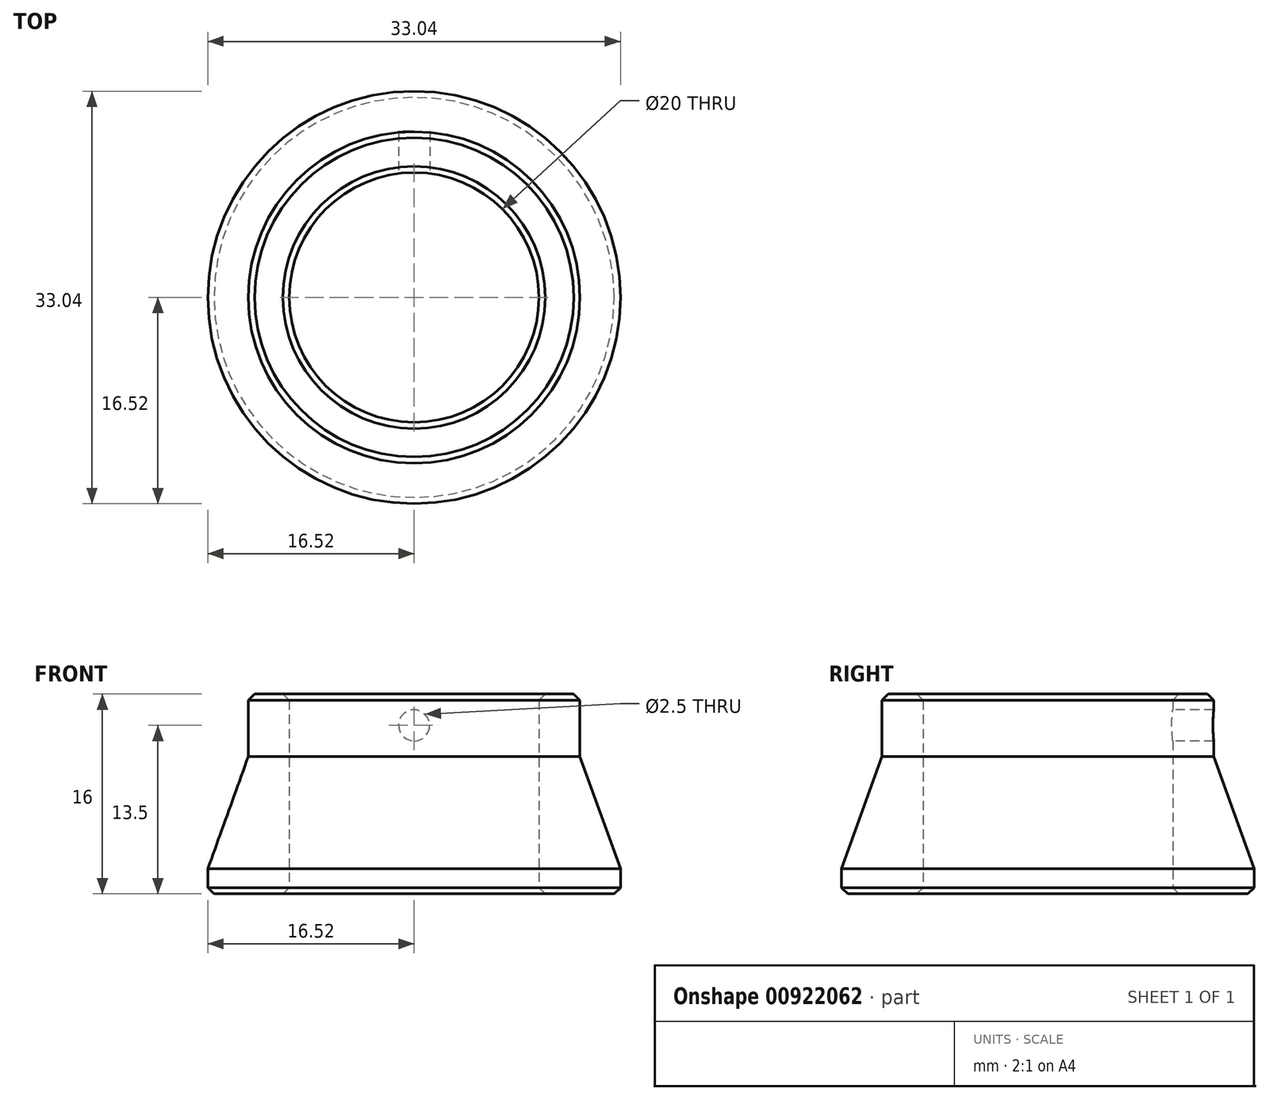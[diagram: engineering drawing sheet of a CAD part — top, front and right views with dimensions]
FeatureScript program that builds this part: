
annotation { "Feature Type Name" : "Feature", "Feature Type Description" : "" }
export const myFeature = defineFeature(function(context is Context, id is Id, definition is map)
    precondition{}
    {
        {
            var Q0;
            Q0=qCreatedBy(makeId("Front.planeOp"),FACE);
            var sketch = newSketch(context, id + "F0", { "sketchPlane" : qUnion([Q0])});
            skLineSegment(sketch, "E0", {"start": v(10, 0) * mm, "end": v(16.52, 0) * mm});
            skLineSegment(sketch, "E1", {"start": v(16.52, 0) * mm, "end": v(16.52, 2) * mm});
            skLineSegment(sketch, "E2", {"start": v(13.28, 15.77) * mm, "end": v(13.28, 16) * mm});
            skLineSegment(sketch, "E3", {"start": v(13.28, 16) * mm, "end": v(10, 16) * mm});
            skLineSegment(sketch, "E4", {"start": v(10, 16) * mm, "end": v(10, 0) * mm});
            skLineSegment(sketch, "E5", {"start": v(13.28, 15.77) * mm, "end": v(13.28, 11) * mm});
            skLineSegment(sketch, "E6", {"start": v(13.28, 11) * mm, "end": v(16.52, 2) * mm});
            skLineSegment(sketch, "E7", {"start": v(0, 0) * mm, "end": v(0, 44.28) * mm, "construction": true});
            skSolve(sketch);
        }
        {
            var Q0;
            Q0=makeQuery(id+"F0.imprint","IMPRINT",FACE,{"disambiguationData":[TD([[makeQuery(id+"F0.imprint","IMPRINT",EDGE,{"derivedFrom":sQuery(id+"F0.wireOp",EDGE,"E0")}),1.0]])]});
            var Q1;
            Q1=sQuery(id+"F0.wireOp",EDGE,"E7");
            revolve(context, id + "F1", {"surfaceOperationType" : NewSurfaceOperationType.NEW, "entities" : qUnion([Q0]), "axis" : qUnion([Q1]), "revolveType" : RevolveType.FULL});
        }
        {
            var Q0;
            Q0=qCreatedBy(makeId("Front.planeOp"),FACE);
            var sketch = newSketch(context, id + "F2", { "sketchPlane" : qUnion([Q0])});
            skPoint(sketch, "E8", {"position": v(0, 13.5) * mm});
            skSolve(sketch);
        }
        {
            var Q0;
            Q0=sQuery(id+"F2.wireOp",VERTEX,"E8");
            var Q1;
            Q1=makeQuery(id+"F1.opRevolve","SWEPT_BODY",BODY,{"disambiguationData":[OSD([sQuery(id+"F0.wireOp",EDGE,"E0"),sQuery(id+"F0.wireOp",EDGE,"E1"),sQuery(id+"F0.wireOp",EDGE,"E2"),sQuery(id+"F0.wireOp",EDGE,"E3"),sQuery(id+"F0.wireOp",EDGE,"E4"),sQuery(id+"F0.wireOp",EDGE,"E5"),sQuery(id+"F0.wireOp",EDGE,"E6")])]});
            hole(context, id + "F3", {"style" : HoleStyle.SIMPLE, "endStyle" : HoleEndStyle.THROUGH, "standardTappedOrClearance" : lookupTablePath({ "standard" : "ISO", "engagement" : "75%", "pitch" : "0.5 mm", "size" : "M3", "type" : "Tapped" }), "standardBlindInLast" : lookupTablePath({ "standard" : "ISO", "engagement" : "75%", "pitch" : "0.5 mm", "size" : "M3", "type" : "Tapped" }), "holeDiameter" : 2.5 * mm, "majorDiameter" : 3 * mm, "showTappedDepth" : true, "isTappedThrough" : true, "tappedDepth" : 6 * mm, "tapClearance" : 3, "locations" : qUnion([Q0]), "scope" : qUnion([Q1])});
        }
        {
            var Q0;
            Q0=makeQuery(id+"F1.opRevolve","SWEPT_EDGE",EDGE,{"disambiguationData":[OSD([sQuery(id+"F0.wireOp",EDGE,"E2"),sQuery(id+"F0.wireOp",EDGE,"E3")])]});
            var Q1;
            Q1=makeQuery(id+"F1.opRevolve","SWEPT_EDGE",EDGE,{"disambiguationData":[OSD([sQuery(id+"F0.wireOp",EDGE,"E3"),sQuery(id+"F0.wireOp",EDGE,"E4")])]});
            var Q2;
            Q2=makeQuery(id+"F1.opRevolve","SWEPT_EDGE",EDGE,{"disambiguationData":[OSD([sQuery(id+"F0.wireOp",EDGE,"E0"),sQuery(id+"F0.wireOp",EDGE,"E4")])]});
            var Q3;
            Q3=makeQuery(id+"F1.opRevolve","SWEPT_EDGE",EDGE,{"disambiguationData":[OSD([sQuery(id+"F0.wireOp",EDGE,"E0"),sQuery(id+"F0.wireOp",EDGE,"E1")])]});
            chamfer(context, id + "F4", {"entities" : qUnion([Q0, Q1, Q2, Q3]), "width" : 0.5 * mm, "tangentPropagation" : true});
        }
    });
